# Revit family: Clevertronics_CWFLED-HV-2IPREM_AUE02820020001
name_source: partatom
category: Lighting Fixtures
units: mm (PartAtom-declared; Revit-internal decimal feet)

## family parameters
Cut with Voids When Loaded = No
Host = Face
Light Source = Yes
Part Type = Normal
Room Calculation Point = No
Round Connector Dimension = Use Diameter
Shared = No

## types (1)
- CWFLED-HV-2IPREM
    Apparent Load = 0 VA
    Clevertronics Base Angle = 0.00°
    Clevertronics_AS2293 Classification = C0=N/A C90=N/A
    Clevertronics_Annotation Size = 0 mm  [stored 0 ft]
    Clevertronics_Battery = 6.4V 3200mAh
    Clevertronics_Battery Type = 2 x Lithium Iron Phosphate
    Clevertronics_Charger Method = Intelligent current limited constant voltage
    Clevertronics_Construction = Polycarbonate
    Clevertronics_Dimensions Main Enclosure = Main enclosure : 380mm x 190mm x 130mm // Lamp : 66mm x 80mm x 206mm
    Clevertronics_Emergency Driver = 8003193 : PCA: RF Node CT10678-A9 Int Antenna Horizontal
    Clevertronics_Emergency LED = 1100550 : WP Led Head, c/w Led's & Loom
    Clevertronics_Height = 130 mm  [stored 0.426509 ft]
    Clevertronics_IP Rating = IP65
    Clevertronics_Length = 380 mm
    Clevertronics_MIC Number = AUE02820020001
    Clevertronics_Material = Clevertronics_Plycarbonate Base
    Clevertronics_Operating Mode = Non-maintained
    Clevertronics_Operating Temperature = -40˚C to 40˚C (remote lamps only), 0˚C to 40˚C (control gear)
    Clevertronics_Operating Voltage = 240V AC; 50Hz
    Clevertronics_Power Consumption = 1.0 Watts (Standby), 5.4 Watts (Max)
    Clevertronics_Product Description = LP Premium LED Weatherproof Supalite flood unit, surface mounted Emergency Light with dual remote lamps
    Clevertronics_Replacement Battery = 1550290 : BATT:LP 6.4V 3.2Ah.200mm lead.Stick.Brkt (2)
    Clevertronics_Testing Node = CCPLED-WP-18V625C-CKIT-HV : LED Power Pack, 18V 625mA, IP Loom,HV,LP (incl HIVE Node)
    Clevertronics_Testing System = Zoneworks XT HIVE (RF)
    Clevertronics_Weight = Main enclosure : 2.6kg // Head - 0.36kg
    Clevertronics_Width = 190 mm
    Color Filter = 16777215
    Default Elevation = 1200 mm
    Description = LP Premium LED Weatherproof Supalite flood unit, surface mounted Emergency Light with dual remote lamps
    Dimming Lamp Color Temperature Shift = <None>
    Lamp = 2 x LED Heads (adjustable), 600lm per lamp head
    Manufacturer = Clevertronics
    Model = CWFLED-HV-2IPREM
    Photometric Web File = ll19823 - CWFLED-ZW.IES
    Tilt Angle = -90.00°

note: [stored X ft] marks values corroborated as IEEE doubles in the binary element streams (Revit-internal decimal feet)

## geometry (parser evidence)
native form markers: Blend x4, Sweep x9
no freeform markers — native parametric forms only
